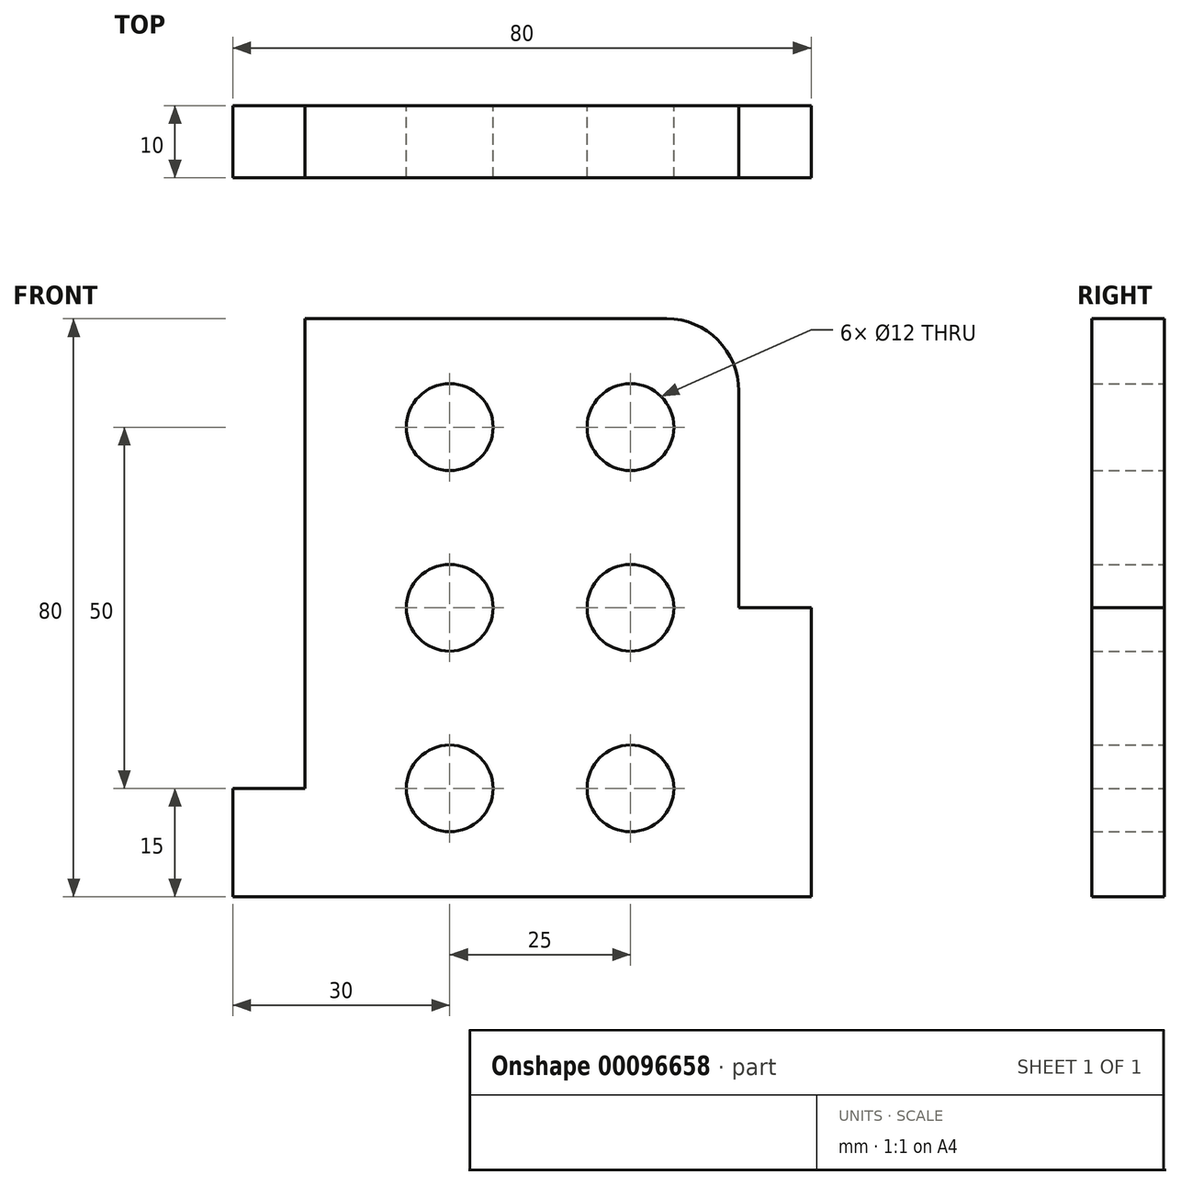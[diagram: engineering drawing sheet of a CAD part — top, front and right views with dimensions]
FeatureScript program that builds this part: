
annotation { "Feature Type Name" : "Feature", "Feature Type Description" : "" }
export const myFeature = defineFeature(function(context is Context, id is Id, definition is map)
    precondition{}
    {
        {
            var Q0;
            Q0=qCreatedBy(makeId("Front.planeOp"),FACE);
            var sketch = newSketch(context, id + "F0", { "sketchPlane" : qUnion([Q0])});
            skLineSegment(sketch, "E0", {"start": v(0, 0) * mm, "end": v(0, 15) * mm});
            skLineSegment(sketch, "E1", {"start": v(0, 15) * mm, "end": v(10, 15) * mm});
            skLineSegment(sketch, "E2", {"start": v(10, 15) * mm, "end": v(10, 80) * mm});
            skLineSegment(sketch, "E3", {"start": v(10, 80) * mm, "end": v(60, 80) * mm});
            skLineSegment(sketch, "E4", {"start": v(70, 70) * mm, "end": v(70, 40) * mm});
            skLineSegment(sketch, "E5", {"start": v(70, 40) * mm, "end": v(80, 40) * mm});
            skLineSegment(sketch, "E6", {"start": v(80, 40) * mm, "end": v(80, 0) * mm});
            skLineSegment(sketch, "E7", {"start": v(80, 0) * mm, "end": v(0, 0) * mm});
            skPoint(sketch, "E8.visualSharp", {"position": v(70, 80) * mm});
            skArc(sketch, "E8.filletArc", {"start": v(70, 70) * mm, "mid": v(67.07, 77.07) * mm, "end": v(60, 80) * mm});
            skLineSegment(sketch, "E9", {"start": v(30, 76.43) * mm, "end": v(30, -11.73) * mm, "construction": true});
            skLineSegment(sketch, "E10", {"start": v(55, 76.43) * mm, "end": v(55, -20.87) * mm, "construction": true});
            skLineSegment(sketch, "E11", {"start": v(16.94, 15) * mm, "end": v(62.63, 15) * mm, "construction": true});
            skLineSegment(sketch, "E12", {"start": v(16.1, 40) * mm, "end": v(62.63, 40) * mm, "construction": true});
            skLineSegment(sketch, "E13", {"start": v(16.1, 65) * mm, "end": v(62.63, 65) * mm, "construction": true});
            skCircle(sketch, "E14", {"center": v(30, 15) * mm, "radius": 6 * mm});
            skCircle(sketch, "E15", {"center": v(55, 15) * mm, "radius": 6 * mm});
            skCircle(sketch, "E16", {"center": v(55, 40) * mm, "radius": 6 * mm});
            skCircle(sketch, "E17", {"center": v(30, 40) * mm, "radius": 6 * mm});
            skCircle(sketch, "E18", {"center": v(30, 65) * mm, "radius": 6 * mm});
            skCircle(sketch, "E19", {"center": v(55, 65) * mm, "radius": 6 * mm});
            skSolve(sketch);
        }
        {
            var Q0;
            Q0 = qSketchRegion(id + "F0", true);
            extrude(context, id + "F1", {"entities" : qUnion([Q0]), "depth" : 10 * mm});
        }
    });
